# Revit family: SEWL-C
name_source: partatom
category: Lighting Fixtures
revit_build: Autodesk Revit Architecture 2012 (Build: 20110309_2315(x64)
units: mm (PartAtom-declared; Revit-internal decimal feet)

## types (1)
- SEWL
    Backbox = White
    Color Filter = 16777215
    Default Elevation = 48.000"
    Description = Exit Sign, Harsh Environment, Die-Cast Aluminum Housing
    Dimming Lamp Color Temperature Shift = <None>
    Emit from Line Length = 14.000"
    Family = Outdoor Emergency Lighting
    Glass = Glass
    Lamp = LED
    Lettering = Red
    Light Source Symbol Size = 0.200"
    Manufacturer = Dual-Lite
    Manufacturer Fax = (864)-678-1415
    Model = SEWL
    Mounting = Wall Mount
    Product Documentation Link = http://www.dual-lite.com
    Product Page URL = http://www.dual-lite.com
    URL = http://www.dual-lite.com
    Wattage Comments = 2.64-3.50W

## geometry (parser evidence)
native form markers: Blend x1, Sweep x1
no freeform markers — native parametric forms only
